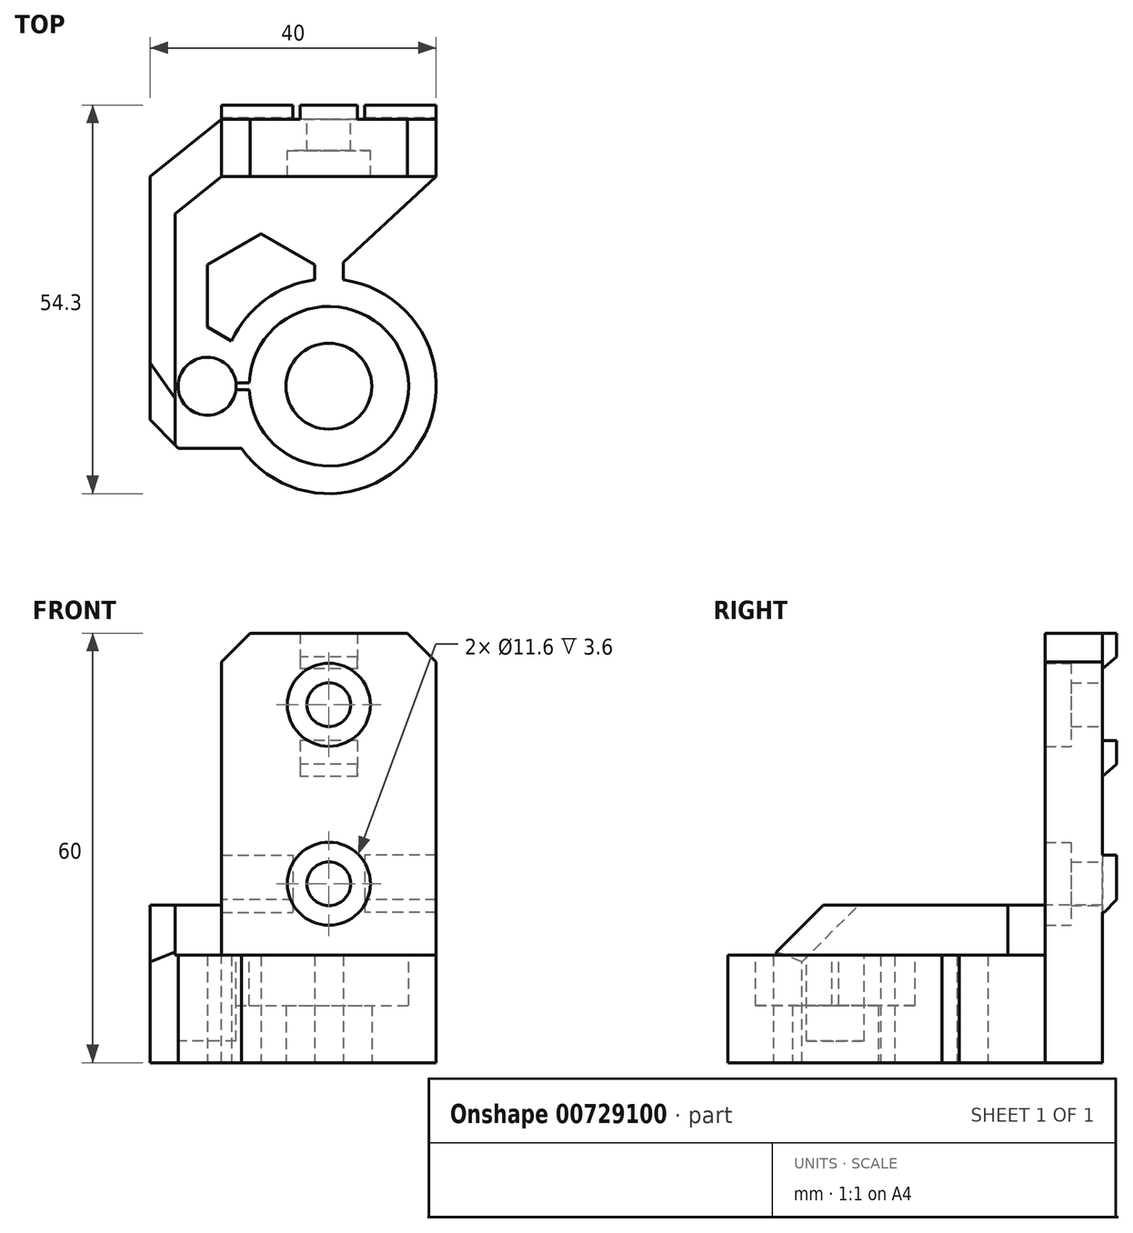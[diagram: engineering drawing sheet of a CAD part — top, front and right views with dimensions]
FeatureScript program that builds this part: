
annotation { "Feature Type Name" : "Feature", "Feature Type Description" : "" }
export const myFeature = defineFeature(function(context is Context, id is Id, definition is map)
    precondition{}
    {
        {
            var Q0;
            Q0=qCreatedBy(makeId("Front.planeOp"),FACE);
            var sketch = newSketch(context, id + "F0", { "sketchPlane" : qUnion([Q0])});
            skLineSegment(sketch, "E0.bottom", {"start": v(0, 0) * mm, "end": v(30, 0) * mm});
            skLineSegment(sketch, "E0.top", {"start": v(0, 60) * mm, "end": v(30, 60) * mm});
            skLineSegment(sketch, "E0.left", {"start": v(0, 0) * mm, "end": v(0, 60) * mm});
            skLineSegment(sketch, "E0.right", {"start": v(30, 0) * mm, "end": v(30, 60) * mm});
            skPoint(sketch, "E1", {"position": v(15, 60) * mm});
            skPoint(sketch, "E2", {"position": v(15, 50) * mm});
            skPoint(sketch, "E3", {"position": v(15, 25) * mm});
            skSolve(sketch);
        }
        {
            var Q0;
            Q0=makeQuery(id+"F0.imprint","IMPRINT",FACE,{"disambiguationData":[TD([[makeQuery(id+"F0.imprint","IMPRINT",EDGE,{"derivedFrom":sQuery(id+"F0.wireOp",EDGE,"E0.bottom")}),1.0]])]});
            extrude(context, id + "F1", {"entities" : qUnion([Q0]), "oppositeDirection" : true, "depth" : 8 * mm, "offsetDistance" : 25 * mm});
        }
        {
            var Q0;
            Q0=sQuery(id+"F0.wireOp",VERTEX,"E2");
            var Q1;
            Q1=sQuery(id+"F0.wireOp",VERTEX,"E3");
            var Q2;
            Q2=makeQuery(id+"F1.opExtrude","SWEPT_BODY",BODY,{"disambiguationData":[OSD([sQuery(id+"F0.wireOp",EDGE,"E0.bottom"),sQuery(id+"F0.wireOp",EDGE,"E0.top"),sQuery(id+"F0.wireOp",EDGE,"E0.left"),sQuery(id+"F0.wireOp",EDGE,"E0.right")])]});
            hole(context, id + "F2", {"style" : HoleStyle.C_BORE, "endStyle" : HoleEndStyle.THROUGH, "holeDiameter" : 6.1 * mm, "cBoreDiameter" : 11.6 * mm, "cBoreDepth" : 3.6 * mm, "majorDiameter" : 5 * mm, "isTappedThrough" : true, "tappedDepth" : 12 * mm, "tapClearance" : 3, "locations" : qUnion([Q0, Q1]), "scope" : qUnion([Q2]), "startStyle" : HoleStartStyle.PART});
        }
        {
            var Q0;
            Q0=makeQuery(id+"F1.opExtrude","SWEPT_FACE",FACE,{"disambiguationData":[OSD([sQuery(id+"F0.wireOp",EDGE,"E0.bottom")])]});
            var sketch = newSketch(context, id + "F3", { "sketchPlane" : qUnion([Q0])});
            skLineSegment(sketch, "E4", {"start": v(30, -8) * mm, "end": v(0, -8) * mm});
            skLineSegment(sketch, "E5", {"start": v(0, -8) * mm, "end": v(-10, 0) * mm});
            skLineSegment(sketch, "E6", {"start": v(-10, 0) * mm, "end": v(-10, 38) * mm});
            skLineSegment(sketch, "E7", {"start": v(-10, 38) * mm, "end": v(2.78, 38) * mm});
            skLineSegment(sketch, "E8", {"start": v(30, -8) * mm, "end": v(30, 0) * mm});
            skLineSegment(sketch, "E9", {"start": v(30, 0) * mm, "end": v(17, 12) * mm});
            skLineSegment(sketch, "E10", {"start": v(17, 12) * mm, "end": v(17, 14.43) * mm});
            skArc(sketch, "E11", {"start": v(2.78, 38) * mm, "mid": v(27.84, 37.05) * mm, "end": v(17, 14.43) * mm});
            skCircle(sketch, "E12", {"center": v(15, 29.3) * mm, "radius": 6 * mm});
            skCircle(sketch, "E13.cCircle", {"center": v(5.5, 16.66) * mm, "radius": 7.5 * mm, "construction": true});
            skLineSegment(sketch, "E13.0", {"start": v(-2, 21) * mm, "end": v(5.5, 25.32) * mm});
            skLineSegment(sketch, "E13.1", {"start": v(5.5, 25.32) * mm, "end": v(13, 21) * mm});
            skLineSegment(sketch, "E13.2", {"start": v(13, 21) * mm, "end": v(13, 12.33) * mm});
            skLineSegment(sketch, "E13.3", {"start": v(13, 12.33) * mm, "end": v(5.5, 8) * mm});
            skLineSegment(sketch, "E13.4", {"start": v(5.5, 8) * mm, "end": v(-2, 12.33) * mm});
            skLineSegment(sketch, "E13.5", {"start": v(-2, 12.33) * mm, "end": v(-2, 21) * mm});
            skPoint(sketch, "E13.0.midPoint", {"position": v(1.75, 23.16) * mm});
            skArc(sketch, "E14", {"start": v(13, 14.43) * mm, "mid": v(6.11, 17.21) * mm, "end": v(1.4, 22.96) * mm});
            skPoint(sketch, "E14.startSnap0", {"position": v(13, 16.66) * mm});
            skSolve(sketch);
        }
        {
            var Q0;
            Q0=makeQuery(id+"F3.imprint","IMPRINT",FACE,{"disambiguationData":[TD([[makeQuery(id+"F3.imprint","IMPRINT",EDGE,{"derivedFrom":sQuery(id+"F3.wireOp",EDGE,"E5")}),-1.0]])]});
            var Q1;
            {var subQ0=sQuery(id+"F3.wireOp",EDGE,"E13.1");Q1=makeQuery(id+"F3.imprint","IMPRINT",FACE,{"disambiguationData":[TD([[makeQuery(id+"F3.imprint","IMPRINT",EDGE,{"derivedFrom":subQ0}),-1.0]])]});}
            extrude(context, id + "F4", {"entities" : qUnion([Q0, Q1]), "operationType" : NewBodyOperationType.ADD, "oppositeDirection" : true, "depth" : 15 * mm, "offsetDistance" : 25 * mm});
        }
        {
            var Q0;
            Q0=makeQuery(id+"F4.opExtrude","CAP_FACE",FACE,{"disambiguationData":[OSD([sQuery(id+"F0.wireOp",EDGE,"E0.bottom"),sQuery(id+"F0.wireOp",EDGE,"E0.left"),sQuery(id+"F3.wireOp",EDGE,"E5"),sQuery(id+"F3.wireOp",EDGE,"E6"),sQuery(id+"F3.wireOp",EDGE,"E7"),sQuery(id+"F3.wireOp",EDGE,"E9"),sQuery(id+"F3.wireOp",EDGE,"E10"),sQuery(id+"F3.wireOp",EDGE,"E11"),sQuery(id+"F3.wireOp",EDGE,"E12"),sQuery(id+"F3.wireOp",EDGE,"E13.0"),sQuery(id+"F3.wireOp",EDGE,"E13.2"),sQuery(id+"F3.wireOp",EDGE,"E13.3"),sQuery(id+"F3.wireOp",EDGE,"E13.4"),sQuery(id+"F3.wireOp",EDGE,"E13.5"),sQuery(id+"F3.wireOp",EDGE,"E14")])],"isStart":false});
            var sketch = newSketch(context, id + "F5", { "sketchPlane" : qUnion([Q0])});
            skPoint(sketch, "E15", {"position": v(-2, -29.3) * mm});
            skPoint(sketch, "E16", {"position": v(15, -29.3) * mm});
            skCircle(sketch, "E17", {"center": v(-2, -29.3) * mm, "radius": 4.05 * mm});
            skCircle(sketch, "E18", {"center": v(15, -29.3) * mm, "radius": 11.15 * mm});
            skLineSegment(sketch, "E19", {"start": v(2.02, -28.8) * mm, "end": v(3.86, -28.8) * mm});
            skLineSegment(sketch, "E20", {"start": v(3.86, -29.8) * mm, "end": v(2.02, -29.8) * mm});
            skSolve(sketch);
        }
        {
            var Q0;
            {var subQ0=sQuery(id+"F5.wireOp",EDGE,"E17");var subQ1=makeQuery(id+"F5.imprint","INTERSECT",VERTEX,{"derivedFrom":[subQ0,sQuery(id+"F5.wireOp",EDGE,"E19")]});Q0=makeQuery(id+"F5.imprint","IMPRINT",FACE,{"disambiguationData":[TD([[makeQuery(id+"F5.imprint","IMPRINT",EDGE,{"disambiguationData":[TD([[subQ1,-1.0]])],"derivedFrom":subQ0}),1.0]])]});}
            extrude(context, id + "F6", {"entities" : qUnion([Q0]), "operationType" : NewBodyOperationType.REMOVE, "oppositeDirection" : true, "depth" : 12 * mm, "offsetDistance" : 25 * mm});
        }
        {
            var Q0;
            Q0=makeQuery(id+"F5.imprint","IMPRINT",FACE,{"disambiguationData":[TD([[makeQuery(id+"F5.imprint","IMPRINT",EDGE,{"derivedFrom":makeQuery(id+"F4.opExtrude","CAP_EDGE",EDGE,{"disambiguationData":[OSD([sQuery(id+"F3.wireOp",EDGE,"E12")])],"isStart":false})}),1.0]])]});
            var Q1;
            {var subQ0=sQuery(id+"F5.wireOp",EDGE,"E19");Q1=makeQuery(id+"F5.imprint","IMPRINT",FACE,{"disambiguationData":[TD([[makeQuery(id+"F5.imprint","IMPRINT",EDGE,{"derivedFrom":subQ0}),-1.0]])]});}
            extrude(context, id + "F7", {"entities" : qUnion([Q0, Q1]), "operationType" : NewBodyOperationType.REMOVE, "oppositeDirection" : true, "depth" : 7 * mm, "offsetDistance" : 25 * mm});
        }
        {
            var Q0;
            {var subQ0=sQuery(id+"F5.wireOp",EDGE,"E19");Q0=makeQuery(id+"F5.imprint","IMPRINT",FACE,{"disambiguationData":[TD([[makeQuery(id+"F5.imprint","IMPRINT",EDGE,{"derivedFrom":subQ0}),1.0]])]});}
            var sketch = newSketch(context, id + "F8", { "sketchPlane" : qUnion([Q0])});
            skLineSegment(sketch, "E21", {"start": v(0, 0) * mm, "end": v(0, 8) * mm});
            skLineSegment(sketch, "E22", {"start": v(0, 8) * mm, "end": v(-10, 0) * mm});
            skLineSegment(sketch, "E23", {"start": v(-10, 0) * mm, "end": v(-10, -38) * mm});
            skLineSegment(sketch, "E24", {"start": v(-10, -38) * mm, "end": v(-6.5, -38) * mm});
            skLineSegment(sketch, "E25", {"start": v(-6.5, -38) * mm, "end": v(-6.5, -5.2) * mm});
            skLineSegment(sketch, "E26", {"start": v(-6.5, -5.2) * mm, "end": v(0, 0) * mm});
            skSolve(sketch);
        }
        {
            var Q0;
            Q0=makeQuery(id+"F8.imprint","IMPRINT",FACE,{"disambiguationData":[TD([[makeQuery(id+"F8.imprint","IMPRINT",EDGE,{"derivedFrom":sQuery(id+"F8.wireOp",EDGE,"E21")}),-1.0]])]});
            extrude(context, id + "F9", {"entities" : qUnion([Q0]), "operationType" : NewBodyOperationType.ADD, "depth" : 7 * mm, "offsetDistance" : 25 * mm});
        }
        {
            var Q0;
            Q0=makeQuery(id+"F9.opExtrude","CAP_EDGE",EDGE,{"disambiguationData":[OSD([sQuery(id+"F8.wireOp",EDGE,"E24")])],"isStart":false});
            chamfer(context, id + "F10", {"entities" : qUnion([Q0]), "width" : 7 * mm, "tangentPropagation" : true});
        }
        {
            var Q0;
            Q0=makeQuery(id+"F1.opExtrude","CAP_FACE",FACE,{"disambiguationData":[OSD([sQuery(id+"F0.wireOp",EDGE,"E0.bottom"),sQuery(id+"F0.wireOp",EDGE,"E0.top"),sQuery(id+"F0.wireOp",EDGE,"E0.left"),sQuery(id+"F0.wireOp",EDGE,"E0.right")])],"isStart":false});
            var sketch = newSketch(context, id + "F11", { "sketchPlane" : qUnion([Q0])});
            skLineSegment(sketch, "E27.bottom", {"start": v(-19, 60) * mm, "end": v(-11, 60) * mm});
            skLineSegment(sketch, "E27.top", {"start": v(-19, 55) * mm, "end": v(-11, 55) * mm});
            skLineSegment(sketch, "E27.left", {"start": v(-19, 60) * mm, "end": v(-19, 55) * mm});
            skLineSegment(sketch, "E27.right", {"start": v(-11, 60) * mm, "end": v(-11, 55) * mm});
            skLineSegment(sketch, "E28.bottom", {"start": v(-19, 45) * mm, "end": v(-11, 45) * mm});
            skLineSegment(sketch, "E28.top", {"start": v(-19, 40) * mm, "end": v(-11, 40) * mm});
            skLineSegment(sketch, "E28.left", {"start": v(-19, 45) * mm, "end": v(-19, 40) * mm});
            skLineSegment(sketch, "E28.right", {"start": v(-11, 45) * mm, "end": v(-11, 40) * mm});
            skLineSegment(sketch, "E29.bottom", {"start": v(-30, 29) * mm, "end": v(-20, 29) * mm});
            skLineSegment(sketch, "E29.top", {"start": v(-30, 21) * mm, "end": v(-20, 21) * mm});
            skLineSegment(sketch, "E29.left", {"start": v(-30, 29) * mm, "end": v(-30, 21) * mm});
            skLineSegment(sketch, "E29.right", {"start": v(-20, 29) * mm, "end": v(-20, 21) * mm});
            skLineSegment(sketch, "E30.bottom", {"start": v(0, 29) * mm, "end": v(-10, 29) * mm});
            skLineSegment(sketch, "E30.top", {"start": v(0, 21) * mm, "end": v(-10, 21) * mm});
            skLineSegment(sketch, "E30.left", {"start": v(0, 29) * mm, "end": v(0, 21) * mm});
            skLineSegment(sketch, "E30.right", {"start": v(-10, 29) * mm, "end": v(-10, 21) * mm});
            skSolve(sketch);
        }
        {
            var Q0;
            Q0=makeQuery(id+"F11.imprint","IMPRINT",FACE,{"disambiguationData":[TD([[makeQuery(id+"F11.imprint","IMPRINT",EDGE,{"derivedFrom":sQuery(id+"F11.wireOp",EDGE,"E27.bottom")}),1.0]])]});
            var Q1;
            Q1=makeQuery(id+"F11.imprint","IMPRINT",FACE,{"disambiguationData":[TD([[makeQuery(id+"F11.imprint","IMPRINT",EDGE,{"derivedFrom":sQuery(id+"F11.wireOp",EDGE,"E28.bottom")}),-1.0]])]});
            var Q2;
            {var subQ2=sQuery(id+"F11.wireOp",EDGE,"E30.bottom");Q2=makeQuery(id+"F11.imprint","IMPRINT",FACE,{"disambiguationData":[TD([[makeQuery(id+"F11.imprint","IMPRINT",EDGE,{"derivedFrom":subQ2}),1.0]])]});}
            var Q3;
            Q3=makeQuery(id+"F11.imprint","IMPRINT",FACE,{"disambiguationData":[TD([[makeQuery(id+"F11.imprint","IMPRINT",EDGE,{"derivedFrom":sQuery(id+"F11.wireOp",EDGE,"E29.bottom")}),-1.0]])]});
            extrude(context, id + "F12", {"entities" : qUnion([Q0, Q1, Q2, Q3]), "operationType" : NewBodyOperationType.ADD, "depth" : 2 * mm, "offsetDistance" : 25 * mm});
        }
        {
            var Q0;
            Q0=makeQuery(id+"F12.opExtrude","CAP_EDGE",EDGE,{"disambiguationData":[OSD([sQuery(id+"F11.wireOp",EDGE,"E27.top")])],"isStart":false});
            var Q1;
            Q1=makeQuery(id+"F12.opExtrude","CAP_EDGE",EDGE,{"disambiguationData":[OSD([sQuery(id+"F11.wireOp",EDGE,"E28.top")])],"isStart":false});
            chamfer(context, id + "F13", {"entities" : qUnion([Q0, Q1]), "chamferType" : ChamferType.OFFSET_ANGLE, "width" : 2 * mm, "oppositeDirection" : true, "angle" : 40 * degree, "tangentPropagation" : true});
        }
        {
            var Q0;
            Q0=makeQuery(id+"F12.opExtrude","CAP_EDGE",EDGE,{"disambiguationData":[OSD([sQuery(id+"F11.wireOp",EDGE,"E29.top")])],"isStart":false});
            var Q1;
            Q1=makeQuery(id+"F12.opExtrude","CAP_EDGE",EDGE,{"disambiguationData":[OSD([sQuery(id+"F11.wireOp",EDGE,"E30.top")])],"isStart":false});
            chamfer(context, id + "F14", {"entities" : qUnion([Q0, Q1]), "chamferType" : ChamferType.OFFSET_ANGLE, "width" : 1.75 * mm, "oppositeDirection" : true, "angle" : 45 * degree, "tangentPropagation" : true});
        }
        {
            var Q0;
            Q0=makeQuery(id+"F9.boolean.opBoolean","MERGE",EDGE,{"derivedFrom":[makeQuery(id+"F4.opExtrude","SWEPT_EDGE",EDGE,{"disambiguationData":[OSD([sQuery(id+"F3.wireOp",EDGE,"E6"),sQuery(id+"F3.wireOp",EDGE,"E7")])]}),makeQuery(id+"F9.opExtrude","SWEPT_EDGE",EDGE,{"disambiguationData":[OSD([sQuery(id+"F8.wireOp",EDGE,"E23"),sQuery(id+"F8.wireOp",EDGE,"E24")])]})]});
            chamfer(context, id + "F15", {"entities" : qUnion([Q0]), "width" : 4 * mm, "tangentPropagation" : true});
        }
        {
            var Q0;
            Q0=makeQuery(id+"F10.opChamfer","BLEND_EDGE",EDGE,{"blendedFrom":[makeQuery(id+"F9.opExtrude","CAP_EDGE",EDGE,{"disambiguationData":[OSD([sQuery(id+"F8.wireOp",EDGE,"E24")])],"isStart":false}),makeQuery(id+"F9.boolean.opBoolean","MERGE",FACE,{"derivedFrom":[makeQuery(id+"F4.opExtrude","SWEPT_FACE",FACE,{"disambiguationData":[OSD([sQuery(id+"F3.wireOp",EDGE,"E6")])]}),makeQuery(id+"F9.opExtrude","SWEPT_FACE",FACE,{"disambiguationData":[OSD([sQuery(id+"F8.wireOp",EDGE,"E23")])]})]})],"blendedInto":[makeQuery(id+"F9.boolean.opBoolean","MERGE",FACE,{"derivedFrom":[makeQuery(id+"F4.opExtrude","SWEPT_FACE",FACE,{"disambiguationData":[OSD([sQuery(id+"F3.wireOp",EDGE,"E6")])]}),makeQuery(id+"F9.opExtrude","SWEPT_FACE",FACE,{"disambiguationData":[OSD([sQuery(id+"F8.wireOp",EDGE,"E23")])]})]})]});
            chamfer(context, id + "F16", {"entities" : qUnion([Q0]), "width" : 3.5 * mm, "tangentPropagation" : true});
        }
        {
            var Q0;
            Q0=makeQuery(id+"F1.opExtrude","SWEPT_EDGE",EDGE,{"disambiguationData":[OSD([sQuery(id+"F0.wireOp",EDGE,"E0.top"),sQuery(id+"F0.wireOp",EDGE,"E0.right")])]});
            var Q1;
            Q1=makeQuery(id+"F1.opExtrude","SWEPT_EDGE",EDGE,{"disambiguationData":[OSD([sQuery(id+"F0.wireOp",EDGE,"E0.top"),sQuery(id+"F0.wireOp",EDGE,"E0.left")])]});
            chamfer(context, id + "F17", {"entities" : qUnion([Q0, Q1]), "width" : 4 * mm, "tangentPropagation" : true});
        }
    });
